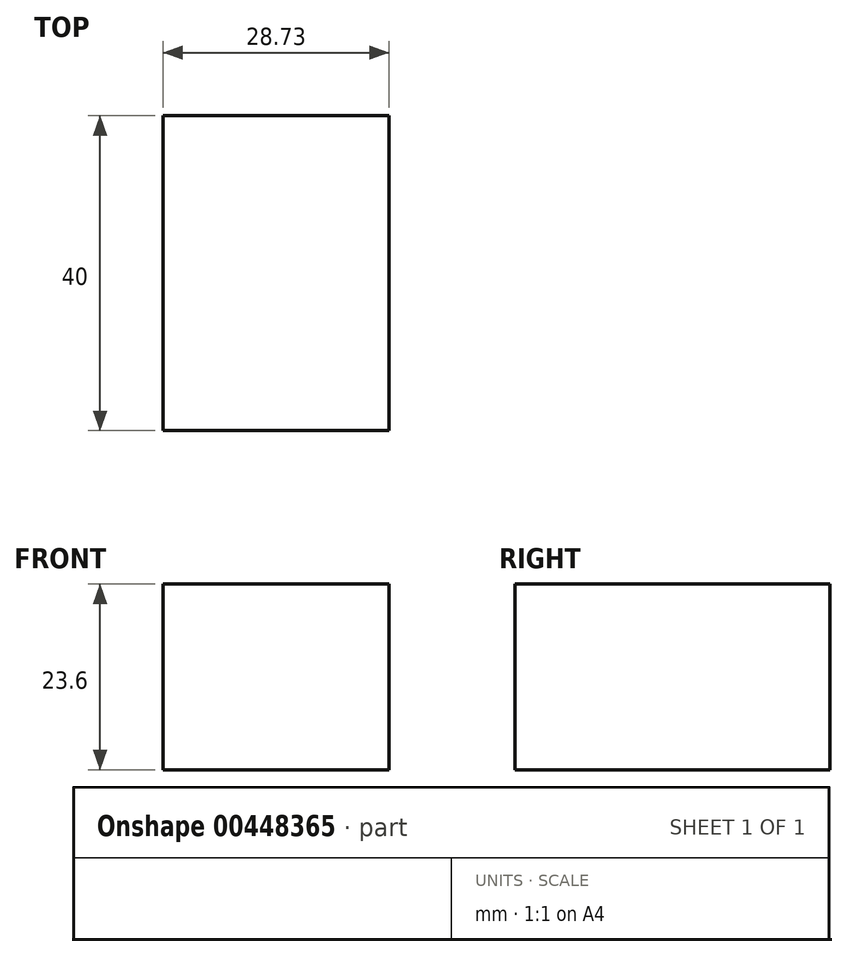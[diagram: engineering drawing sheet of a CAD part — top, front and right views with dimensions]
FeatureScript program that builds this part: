
annotation { "Feature Type Name" : "Feature", "Feature Type Description" : "" }
export const myFeature = defineFeature(function(context is Context, id is Id, definition is map)
    precondition{}
    {
        {
            var Q0;
            Q0=qCreatedBy(makeId("Front.planeOp"),FACE);
            var sketch = newSketch(context, id + "F0", { "sketchPlane" : qUnion([Q0])});
            skLineSegment(sketch, "E0.bottom", {"start": v(23.85, 36.3) * mm, "end": v(-4.88, 36.3) * mm});
            skLineSegment(sketch, "E0.top", {"start": v(23.85, 12.7) * mm, "end": v(-4.88, 12.7) * mm});
            skLineSegment(sketch, "E0.left", {"start": v(23.85, 36.3) * mm, "end": v(23.85, 12.7) * mm});
            skLineSegment(sketch, "E0.right", {"start": v(-4.88, 36.3) * mm, "end": v(-4.88, 12.7) * mm});
            skSolve(sketch);
        }
        {
            var Q0;
            Q0=makeQuery(id+"F0.imprint","IMPRINT",FACE,{"disambiguationData":[TD([[makeQuery(id+"F0.imprint","IMPRINT",EDGE,{"derivedFrom":sQuery(id+"F0.wireOp",EDGE,"E0.bottom")}),1.0]])]});
            extrude(context, id + "F1", {"entities" : qUnion([Q0]), "depth" : 40 * mm});
        }
    });
